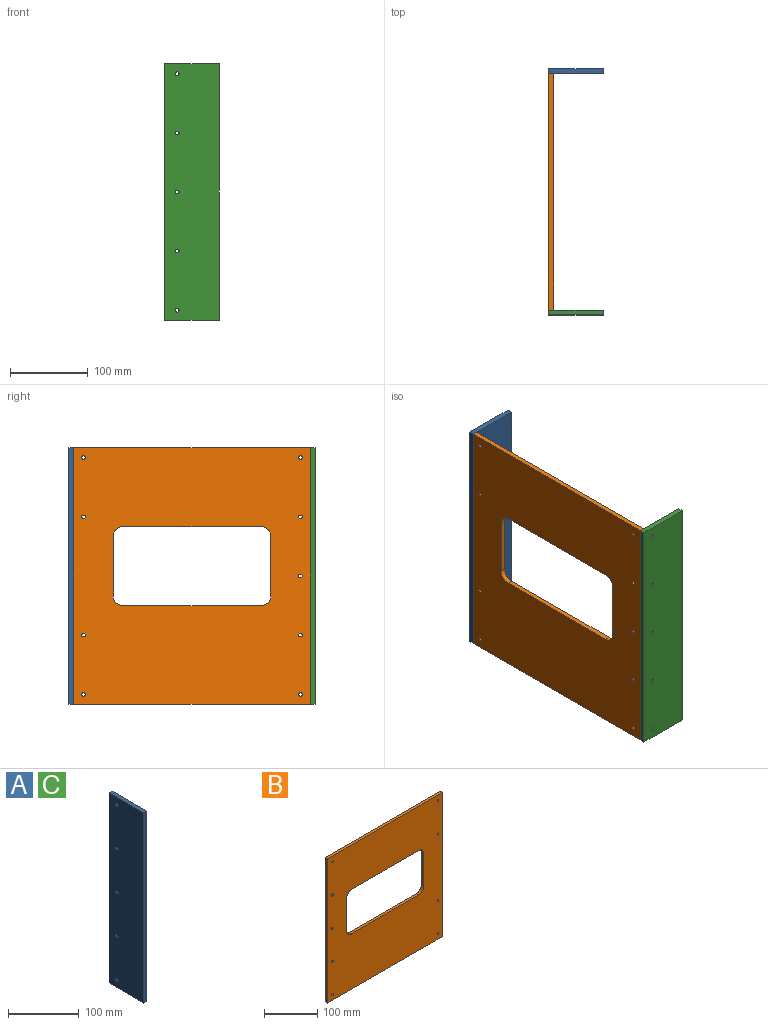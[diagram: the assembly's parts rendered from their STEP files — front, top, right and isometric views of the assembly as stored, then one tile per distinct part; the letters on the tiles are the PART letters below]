
ASSEMBLY  parts=3 mates=1
PART A: 11 faces, bbox 6.4x69.9x330.2 mm
  f0: plane 69.85x6.35mm, normal (0,0,1), area 443.5mm2, adj f1,f3,f4,f5
  f1: plane 330.2x6.35mm, normal (0,-1,0), area 2096.8mm2, adj f0,f2,f4,f5
  f2: plane 69.85x6.35mm, normal (0,0,-1), area 443.5mm2, adj f1,f3,f4,f5
  f3: plane 330.2x6.35mm, normal (0,1,0), area 2096.8mm2, adj f0,f2,f4,f5
  f4: plane 330.2x69.85mm, normal (1,0,0), area 22975.4mm2, adj f0,f1,f2,f3,f6,f7,f8,f9
  f5: plane 330.2x69.85mm, normal (-1,0,0), area 22975.4mm2, adj f0,f1,f2,f3,f6,f7,f8,f9
  f6: cylinder r=2.38mm len=6.35mm, axis (-1,0,0), area 95mm2, adj f4,f5
  f7: cylinder r=2.38mm len=6.35mm, axis (-1,0,0), area 95mm2, adj f4,f5
  f8: cylinder r=2.38mm len=6.35mm, axis (-1,0,0), area 95mm2, adj f4,f5
  f9: cylinder r=2.38mm len=6.35mm, axis (-1,0,0), area 95mm2, adj f4,f5
  f10: cylinder r=2.38mm len=6.35mm, axis (-1,0,0), area 95mm2, adj f4,f5
PART B: 23 faces, bbox 304.8x6.4x330.2 mm
  f0: plane 330.2x304.8mm, normal (0,-1,0), area 79978mm2, adj f2,f3,f4,f5,f6,f7,f8,f9
  f1: plane 330.2x304.8mm, normal (0,1,0), area 79978mm2, adj f2,f3,f4,f5,f6,f7,f8,f9
  f2: plane 304.8x6.35mm, normal (0,0,1), area 1935.5mm2, adj f0,f1,f4,f5
  f3: plane 304.8x6.35mm, normal (0,0,-1), area 1935.5mm2, adj f0,f1,f4,f5
  f4: plane 330.2x6.35mm, normal (-1,0,0), area 2096.8mm2, adj f0,f1,f2,f3
  f5: plane 330.2x6.35mm, normal (1,0,0), area 2096.8mm2, adj f0,f1,f2,f3
  f6: plane 177.8x6.35mm, normal (0,0,-1), area 1129mm2, adj f0,f1,f7,f13
  f7: cylinder r=12.7mm len=12.7mm, axis (0,-1,0), area 126.7mm2, adj f0,f1,f6,f8
  f8: plane 76.2x6.35mm, normal (1,0,0), area 483.9mm2, adj f0,f1,f7,f9
  f9: cylinder r=12.7mm len=12.7mm, axis (0,-1,0), area 126.7mm2, adj f0,f1,f8,f10
  f10: plane 177.8x6.35mm, normal (0,0,1), area 1129mm2, adj f0,f1,f9,f11
  f11: cylinder r=12.7mm len=12.7mm, axis (0,-1,0), area 126.7mm2, adj f0,f1,f10,f12
  f12: plane 76.2x6.35mm, normal (-1,0,0), area 483.9mm2, adj f0,f1,f11,f13
  f13: cylinder r=12.7mm len=12.7mm, axis (0,-1,0), area 126.7mm2, adj f0,f1,f6,f12
  f14: cylinder r=2.38mm len=6.35mm, axis (0,-1,0), area 95mm2, adj f0,f1
  f15: cylinder r=2.38mm len=6.35mm, axis (0,-1,0), area 95mm2, adj f0,f1
  f16: cylinder r=2.38mm len=6.35mm, axis (0,-1,0), area 95mm2, adj f0,f1
  f17: cylinder r=2.38mm len=6.35mm, axis (0,-1,0), area 95mm2, adj f0,f1
  f18: cylinder r=2.38mm len=6.35mm, axis (0,-1,0), area 95mm2, adj f0,f1
  f19: cylinder r=2.38mm len=6.35mm, axis (0,-1,0), area 95mm2, adj f0,f1
  f20: cylinder r=2.38mm len=6.35mm, axis (0,-1,0), area 95mm2, adj f0,f1
  f21: cylinder r=2.38mm len=6.35mm, axis (0,-1,0), area 95mm2, adj f0,f1
  f22: cylinder r=2.38mm len=6.35mm, axis (0,-1,0), area 95mm2, adj f0,f1
PART C: same geometry as A
PLACE A rot(axis=(0,0,1),90deg) t=(0,158.75,202.22)mm
PLACE B rot(axis=(0,0,1),90deg) t=(0,158.75,202.22)mm
PLACE C rot(axis=(0,0,1),90deg) t=(0,-152.4,202.22)mm
MATE fastened A.f5 <-> B.f5  axis (0,-1,0) through (-38.1,311.15,37.12)mm
